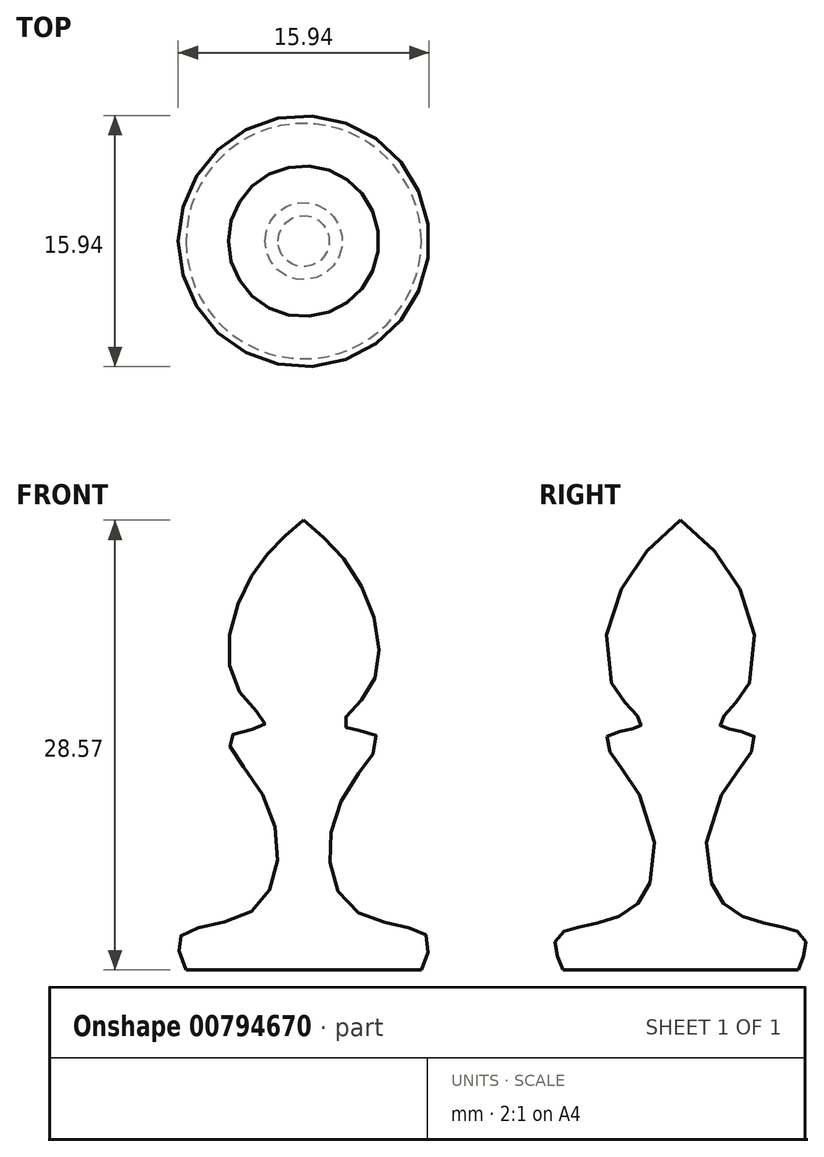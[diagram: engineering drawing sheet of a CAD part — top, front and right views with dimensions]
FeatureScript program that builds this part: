
annotation { "Feature Type Name" : "Feature", "Feature Type Description" : "" }
export const myFeature = defineFeature(function(context is Context, id is Id, definition is map)
    precondition{}
    {
        {
            var Q0;
            Q0=qCreatedBy(makeId("Top.planeOp"),FACE);
            var sketch = newSketch(context, id + "F0", { "sketchPlane" : qUnion([Q0])});
            skCircle(sketch, "E0", {"center": v(0, 0) * mm, "radius": 7.7 * mm});
            skSolve(sketch);
        }
        {
            var Q0;
            Q0=qCreatedBy(makeId("Front.planeOp"),FACE);
            var sketch = newSketch(context, id + "F1", { "sketchPlane" : qUnion([Q0])});
            skFitSpline(sketch, "E1", {"points": [v(7.47, 0) * mm, v(7.76, 2.21) * mm, v(3.16, 3.83) * mm, v(2.3, 10.56) * mm, v(4.68, 14.82) * mm, v(2.5, 15.53) * mm, v(4.35, 18.14) * mm, v(3.4, 24.87) * mm, v(0, 28.57) * mm], "startDerivative": vector(12.39, 29.14) * mm, "endDerivative": vector(-27.11, 22.55) * mm});
            skLineSegment(sketch, "E2", {"start": v(0, 28.57) * mm, "end": v(0, 0) * mm});
            skLineSegment(sketch, "E3", {"start": v(0, 0) * mm, "end": v(7.47, 0) * mm});
            skSolve(sketch);
        }
        {
            var Q0;
            Q0=makeQuery(id+"F1.imprint","IMPRINT",FACE,{"disambiguationData":[TD([[makeQuery(id+"F1.imprint","IMPRINT",EDGE,{"derivedFrom":sQuery(id+"F1.wireOp",EDGE,"E1")}),1.0]])]});
            var Q1;
            Q1=sQuery(id+"F0.wireOp",EDGE,"E0");
            sweep(context, id + "F2", {"profiles" : qUnion([Q0]), "path" : qUnion([Q1])});
        }
    });
